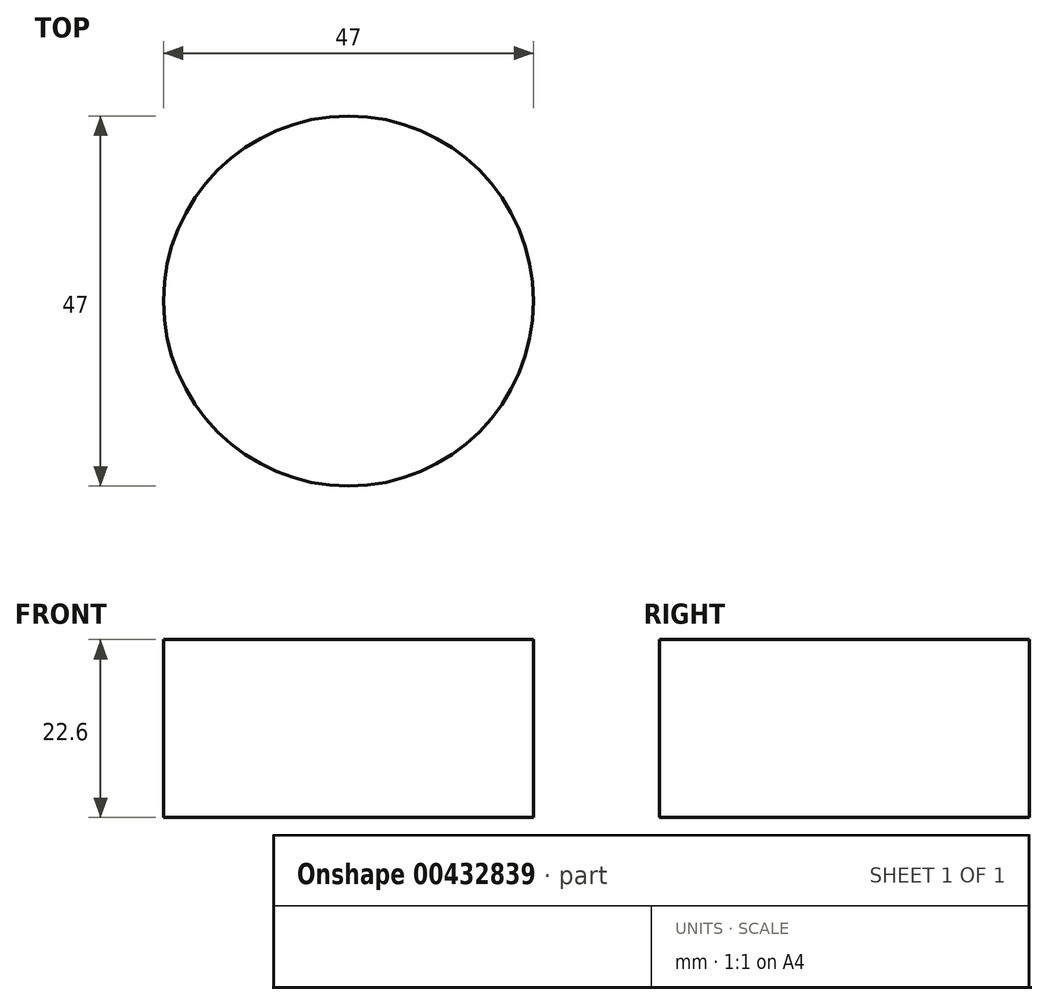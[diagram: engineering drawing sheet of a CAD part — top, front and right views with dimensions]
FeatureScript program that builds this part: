
annotation { "Feature Type Name" : "Feature", "Feature Type Description" : "" }
export const myFeature = defineFeature(function(context is Context, id is Id, definition is map)
    precondition{}
    {
        {
            var Q0;
            Q0=qCreatedBy(makeId("Top.planeOp"),FACE);
            var sketch = newSketch(context, id + "F0", { "sketchPlane" : qUnion([Q0])});
            skCircle(sketch, "E0", {"center": v(0, 0) * mm, "radius": 23.5 * mm});
            skSolve(sketch);
        }
        {
            var Q0;
            Q0 = qSketchRegion(id + "F0", true);
            extrude(context, id + "F1", {"entities" : qUnion([Q0]), "depth" : 22.6 * mm});
        }
    });
